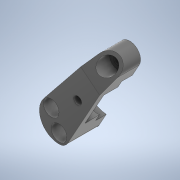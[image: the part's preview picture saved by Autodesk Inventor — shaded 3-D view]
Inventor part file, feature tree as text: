
AUTODESK INVENTOR PART (.ipt)
format: ipt  version: 2022 (Build 260153000, 153)  size: 220,160 bytes
history: native  units: mm
features: extrude x5, sketch x5
ambient origin geometry x8: Origin, YZ Plane, XZ Plane, XY Plane, X Axis, Y Axis, Z Axis, Center Point
bodies: Solid1 (feature_tree)
feature tree (10):
  extrude  "Extrusion1"  Depth=24.0mm
  extrude  "Extrusion2"  Depth=3.0mm
  extrude  "Extrusion3"  Depth=2.1mm
  extrude  "Extrusion4"  Depth=2.5mm
  extrude  "Extrusion5"  Depth=10.0mm
  sketch  "Sketch1"  dims[d0=18.0mm d1=24.0mm]
  sketch  "Sketch3"  dims[d2=2.1mm d3=3.0mm]
  sketch  "Sketch5"  dims[d4=3.0mm d5=2.1mm]
  sketch  "Sketch6"  dims[d6=2.1mm d7=2.5mm]
  sketch  "Sketch8"  dims[d8=5.0mm d9=3.0mm d10=7.0mm d12=10.0mm d15=6.0mm d16=8.0mm d17=0.0mm d18=2.0mm d25=5.5mm d26=10.0mm d27=14.9mm d28=2.7mm d29=0.0mm d30=12.0mm d31=8.251mm d32=4.0mm d33=4.0mm d34=4.0mm d35=4.9mm d36=0.0mm d37=11.4mm d38=3.65mm d39=0.0mm d40=10.0mm d41=0.0mm]
